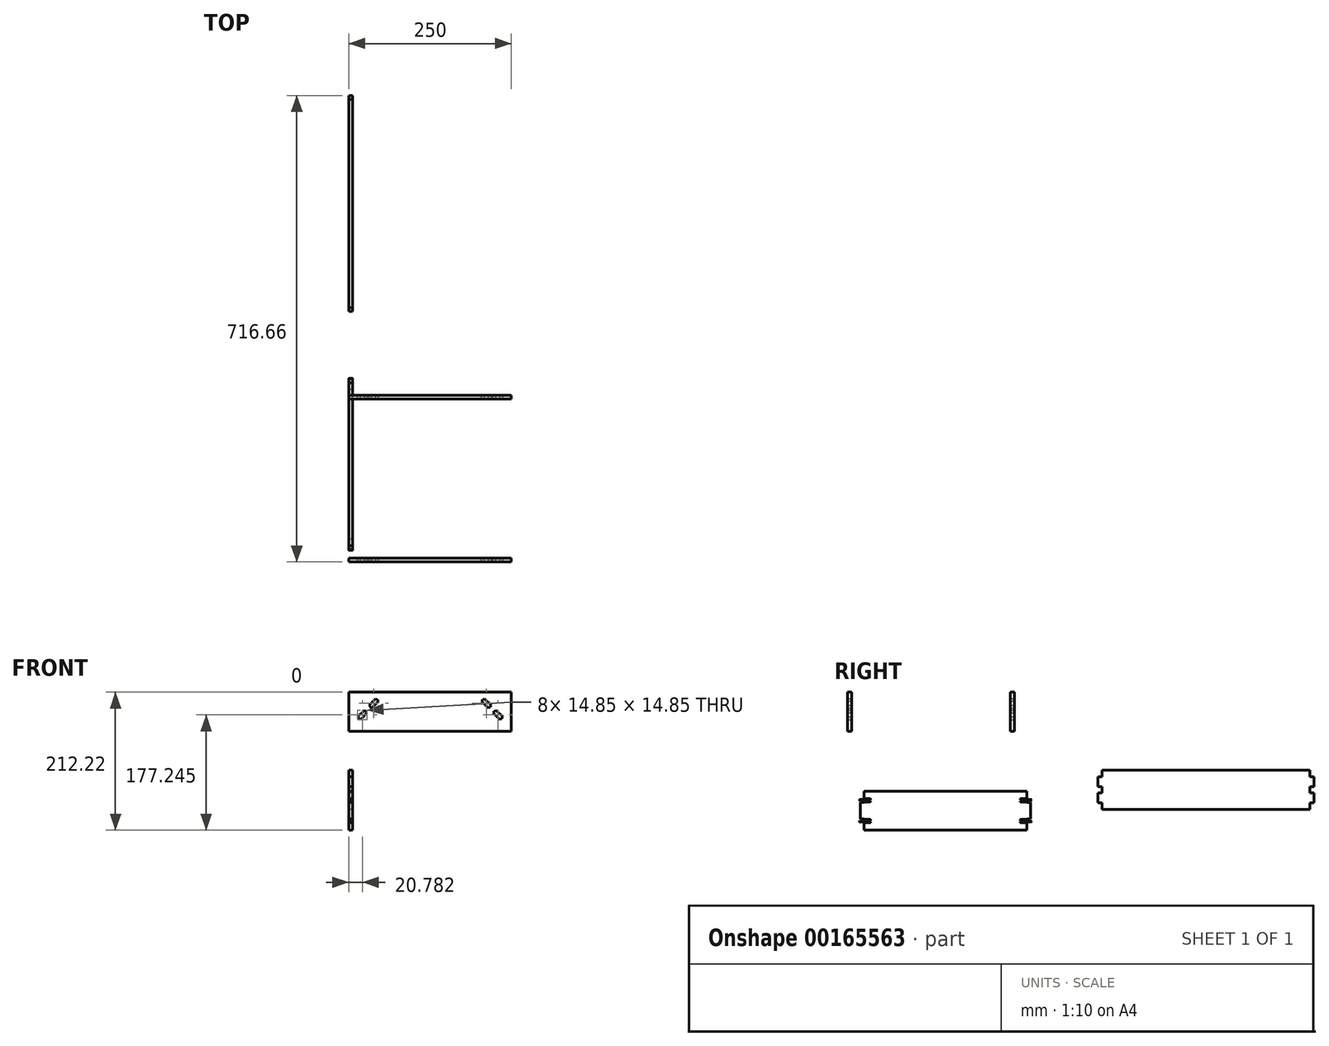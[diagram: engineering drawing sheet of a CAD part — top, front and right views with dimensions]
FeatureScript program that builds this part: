
annotation { "Feature Type Name" : "Feature", "Feature Type Description" : "" }
export const myFeature = defineFeature(function(context is Context, id is Id, definition is map)
    precondition{}
    {
        {
            assignVariable(context, id + "F0", {"name" : "t", "anyValue" : 6});
        }
        {
            assignVariable(context, id + "F1", {"name" : "w", "anyValue" : 250});
        }
        {
            var Q0;
            Q0=qCreatedBy(makeId("Front.planeOp"),FACE);
            var sketch = newSketch(context, id + "F2", { "sketchPlane" : qUnion([Q0])});
            skLineSegment(sketch, "E0.bottom", {"start": v(0, 0) * mm, "end": v(250, 0) * mm});
            skLineSegment(sketch, "E0.top", {"start": v(0, 60) * mm, "end": v(250, 60) * mm});
            skLineSegment(sketch, "E0.left", {"start": v(0, 0) * mm, "end": v(0, 60) * mm});
            skLineSegment(sketch, "E0.right", {"start": v(250, 0) * mm, "end": v(250, 60) * mm});
            skLineSegment(sketch, "E1.bottom", {"start": v(17.6, 17.6) * mm, "end": v(28.2, 28.2) * mm});
            skLineSegment(sketch, "E1.top", {"start": v(13.36, 21.84) * mm, "end": v(23.96, 32.45) * mm});
            skLineSegment(sketch, "E1.left", {"start": v(17.6, 17.6) * mm, "end": v(13.36, 21.84) * mm});
            skLineSegment(sketch, "E1.right", {"start": v(28.2, 28.2) * mm, "end": v(23.96, 32.45) * mm});
            skLineSegment(sketch, "E2.1.0.0", {"start": v(45.88, 45.88) * mm, "end": v(41.64, 50.13) * mm});
            skLineSegment(sketch, "E2.1.0.1", {"start": v(31.04, 39.52) * mm, "end": v(41.64, 50.13) * mm});
            skLineSegment(sketch, "E2.1.0.2", {"start": v(35.28, 35.28) * mm, "end": v(45.88, 45.88) * mm});
            skLineSegment(sketch, "E2.1.0.3", {"start": v(35.28, 35.28) * mm, "end": v(31.04, 39.52) * mm});
            skLineSegment(sketch, "E2.direction1", {"start": v(17.6, 17.6) * mm, "end": v(35.28, 35.28) * mm, "construction": true});
            skLineSegment(sketch, "E3", {"start": v(125, 48.06) * mm, "end": v(125, 16.76) * mm, "construction": true});
            skPoint(sketch, "E3.startSnap0", {"position": v(125, 60) * mm});
            skLineSegment(sketch, "E4.MirrorCS", {"start": v(221.8, 28.2) * mm, "end": v(226.04, 32.45) * mm});
            skLineSegment(sketch, "E5.MirrorCS", {"start": v(214.72, 35.28) * mm, "end": v(218.96, 39.52) * mm});
            skLineSegment(sketch, "E6.MirrorCS", {"start": v(232.4, 17.6) * mm, "end": v(221.8, 28.2) * mm});
            skLineSegment(sketch, "E7.MirrorCS", {"start": v(236.64, 21.84) * mm, "end": v(226.04, 32.45) * mm});
            skLineSegment(sketch, "E8.MirrorCS", {"start": v(232.4, 17.6) * mm, "end": v(236.64, 21.84) * mm});
            skLineSegment(sketch, "E9.MirrorCS", {"start": v(214.72, 35.28) * mm, "end": v(204.12, 45.88) * mm});
            skLineSegment(sketch, "E10.MirrorCS", {"start": v(204.12, 45.88) * mm, "end": v(208.36, 50.13) * mm});
            skLineSegment(sketch, "E11.MirrorCS", {"start": v(218.96, 39.52) * mm, "end": v(208.36, 50.13) * mm});
            skSolve(sketch);
        }
        {
            var Q0;
            Q0=makeQuery(id+"F2.imprint","IMPRINT",FACE,{"disambiguationData":[TD([[makeQuery(id+"F2.imprint","IMPRINT",EDGE,{"derivedFrom":sQuery(id+"F2.wireOp",EDGE,"E0.bottom")}),1.0]])]});
            extrude(context, id + "F3", {"entities" : qUnion([Q0]), "depth" : (getVariable(context, 't')) * mm});
        }
        {
            var Q0;
            Q0=makeQuery(id+"F3.opExtrude","SWEPT_BODY",BODY,{"disambiguationData":[OSD([sQuery(id+"F2.wireOp",EDGE,"E0.bottom"),sQuery(id+"F2.wireOp",EDGE,"E0.top"),sQuery(id+"F2.wireOp",EDGE,"E0.left"),sQuery(id+"F2.wireOp",EDGE,"E0.right")])]});
            transform(context, id + "F4", {"entities" : qUnion([Q0]), "transformType" : TransformType.TRANSLATION_3D, "dx" : 0 * mm, "dy" : (getVariable(context, 'w')) * mm, "dz" : 0 * mm, "makeCopy" : true});
        }
        {
            var Q0;
            Q0=qCreatedBy(makeId("Right.planeOp"),FACE);
            var sketch = newSketch(context, id + "F5", { "sketchPlane" : qUnion([Q0])});
            skLineSegment(sketch, "E12.bottom", {"start": v(19.14, -92.22) * mm, "end": v(269.14, -92.22) * mm});
            skLineSegment(sketch, "E12.top", {"start": v(19.14, -152.22) * mm, "end": v(269.14, -152.22) * mm});
            skLineSegment(sketch, "E12.left", {"start": v(19.14, -92.22) * mm, "end": v(19.14, -103.72) * mm});
            skLineSegment(sketch, "E13", {"start": v(19.14, -122.22) * mm, "end": v(269.14, -122.22) * mm, "construction": true});
            skLineSegment(sketch, "E14", {"start": v(144.14, -92.22) * mm, "end": v(144.14, -152.22) * mm, "construction": true});
            skLineSegment(sketch, "E15", {"start": v(13.14, -109.72) * mm, "end": v(19.14, -109.72) * mm});
            skLineSegment(sketch, "E16", {"start": v(19.14, -107.22) * mm, "end": v(13.14, -107.22) * mm});
            skLineSegment(sketch, "E17", {"start": v(13.14, -105.22) * mm, "end": v(19.14, -105.22) * mm});
            skLineSegment(sketch, "E18", {"start": v(12.05, -105.87) * mm, "end": v(13.14, -107.22) * mm});
            skLineSegment(sketch, "E19", {"start": v(19.14, -107.22) * mm, "end": v(28.38, -107.22) * mm});
            skLineSegment(sketch, "E20", {"start": v(28.38, -108.72) * mm, "end": v(19.14, -108.72) * mm});
            skLineSegment(sketch, "E21", {"start": v(19.14, -108.72) * mm, "end": v(19.14, -109.72) * mm});
            skLineSegment(sketch, "E22", {"start": v(19.14, -105.22) * mm, "end": v(28.38, -105.22) * mm});
            skArc(sketch, "E23", {"start": v(28.38, -105.22) * mm, "mid": v(29.13, -104.47) * mm, "end": v(28.38, -103.72) * mm});
            skArc(sketch, "E24", {"start": v(28.38, -108.72) * mm, "mid": v(29.13, -107.97) * mm, "end": v(28.38, -107.22) * mm});
            skPoint(sketch, "E25.visualSharp", {"position": v(12.44, -104.52) * mm});
            skPoint(sketch, "E26.visualSharp", {"position": v(11.9, -105.69) * mm});
            skLineSegment(sketch, "E27", {"start": v(13.14, -109.72) * mm, "end": v(13.14, -122.22) * mm});
            skLineSegment(sketch, "E28", {"start": v(13.14, -105.22) * mm, "end": v(12.66, -104.75) * mm});
            skLineSegment(sketch, "E29", {"start": v(12.02, -105.68) * mm, "end": v(12.33, -104.82) * mm});
            skArc(sketch, "E30.filletArc", {"start": v(12.66, -104.75) * mm, "mid": v(12.48, -104.7) * mm, "end": v(12.33, -104.82) * mm});
            skPoint(sketch, "E31.visualSharp", {"position": v(11.98, -105.78) * mm});
            skArc(sketch, "E31.filletArc", {"start": v(12.02, -105.68) * mm, "mid": v(12, -105.78) * mm, "end": v(12.05, -105.87) * mm});
            skLineSegment(sketch, "E32", {"start": v(13.14, -122.22) * mm, "end": v(13.14, -134.72) * mm});
            skLineSegment(sketch, "E33", {"start": v(13.14, -134.72) * mm, "end": v(19.14, -134.72) * mm});
            skPoint(sketch, "E34", {"position": v(19.14, -134.72) * mm});
            skLineSegment(sketch, "E35.trimOffspring", {"start": v(19.14, -134.72) * mm, "end": v(19.14, -134.72) * mm});
            skLineSegment(sketch, "E36", {"start": v(28.38, -103.72) * mm, "end": v(19.14, -103.72) * mm});
            skArc(sketch, "E37.MirrorCS", {"start": v(12.66, -139.69) * mm, "mid": v(12.48, -139.74) * mm, "end": v(12.33, -139.61) * mm});
            skLineSegment(sketch, "E38.MirrorCS", {"start": v(13.14, -139.2) * mm, "end": v(12.66, -139.69) * mm});
            skLineSegment(sketch, "E39.MirrorCS", {"start": v(12.02, -138.75) * mm, "end": v(12.33, -139.61) * mm});
            skArc(sketch, "E40.MirrorCS", {"start": v(12.02, -138.75) * mm, "mid": v(12, -138.65) * mm, "end": v(12.05, -138.56) * mm});
            skPoint(sketch, "E41.MirrorP", {"position": v(12.44, -139.9) * mm});
            skArc(sketch, "E42.MirrorCS", {"start": v(28.38, -135.7) * mm, "mid": v(29.13, -136.46) * mm, "end": v(28.38, -137.2) * mm});
            skLineSegment(sketch, "E43.MirrorCS", {"start": v(12.05, -138.56) * mm, "end": v(13.14, -137.2) * mm});
            skLineSegment(sketch, "E44.MirrorCS", {"start": v(19.14, -135.7) * mm, "end": v(19.14, -134.7) * mm});
            skArc(sketch, "E45.MirrorCS", {"start": v(28.38, -139.2) * mm, "mid": v(29.13, -139.96) * mm, "end": v(28.38, -140.7) * mm});
            skPoint(sketch, "E46.MirrorP", {"position": v(11.98, -138.65) * mm});
            skPoint(sketch, "E47.MirrorP", {"position": v(11.9, -138.74) * mm});
            skLineSegment(sketch, "E48.MirrorCS", {"start": v(19.14, -137.2) * mm, "end": v(13.14, -137.2) * mm});
            skLineSegment(sketch, "E49.MirrorCS", {"start": v(19.14, -137.2) * mm, "end": v(28.38, -137.2) * mm});
            skLineSegment(sketch, "E50.MirrorCS", {"start": v(28.38, -135.7) * mm, "end": v(19.14, -135.7) * mm});
            skLineSegment(sketch, "E51.MirrorCS", {"start": v(19.14, -139.2) * mm, "end": v(28.38, -139.2) * mm});
            skLineSegment(sketch, "E52.MirrorCS", {"start": v(19.14, -152.22) * mm, "end": v(19.14, -140.7) * mm});
            skLineSegment(sketch, "E53.MirrorCS", {"start": v(13.14, -139.2) * mm, "end": v(19.14, -139.2) * mm});
            skLineSegment(sketch, "E54.MirrorCS", {"start": v(28.38, -140.7) * mm, "end": v(19.14, -140.7) * mm});
            skLineSegment(sketch, "E55.trimOffspring", {"start": v(19.14, -140.7) * mm, "end": v(19.14, -152.22) * mm});
            skLineSegment(sketch, "E56.MirrorCS", {"start": v(275.14, -105.22) * mm, "end": v(275.62, -104.75) * mm});
            skArc(sketch, "E57.MirrorCS", {"start": v(276.26, -105.68) * mm, "mid": v(276.27, -105.78) * mm, "end": v(276.23, -105.87) * mm});
            skArc(sketch, "E58.MirrorCS", {"start": v(275.62, -139.69) * mm, "mid": v(275.8, -139.74) * mm, "end": v(275.95, -139.61) * mm});
            skLineSegment(sketch, "E59.MirrorCS", {"start": v(276.23, -105.87) * mm, "end": v(275.14, -107.22) * mm});
            skLineSegment(sketch, "E60.MirrorCS", {"start": v(276.26, -105.68) * mm, "end": v(275.95, -104.82) * mm});
            skArc(sketch, "E61.MirrorCS", {"start": v(275.62, -104.75) * mm, "mid": v(275.8, -104.7) * mm, "end": v(275.95, -104.82) * mm});
            skLineSegment(sketch, "E62.MirrorCS", {"start": v(276.23, -138.56) * mm, "end": v(275.14, -137.2) * mm});
            skLineSegment(sketch, "E63.MirrorCS", {"start": v(275.14, -139.2) * mm, "end": v(275.62, -139.69) * mm});
            skLineSegment(sketch, "E64.MirrorCS", {"start": v(276.26, -138.75) * mm, "end": v(275.95, -139.61) * mm});
            skArc(sketch, "E65.MirrorCS", {"start": v(276.26, -138.75) * mm, "mid": v(276.27, -138.65) * mm, "end": v(276.23, -138.56) * mm});
            skLineSegment(sketch, "E66.MirrorCS", {"start": v(269.14, -134.72) * mm, "end": v(269.14, -134.72) * mm});
            skLineSegment(sketch, "E67.MirrorCS", {"start": v(269.14, -135.7) * mm, "end": v(269.14, -134.7) * mm});
            skArc(sketch, "E68.MirrorCS", {"start": v(259.9, -108.72) * mm, "mid": v(259.15, -107.97) * mm, "end": v(259.9, -107.22) * mm});
            skLineSegment(sketch, "E69.MirrorCS", {"start": v(269.14, -107.22) * mm, "end": v(275.14, -107.22) * mm});
            skArc(sketch, "E70.MirrorCS", {"start": v(259.9, -135.7) * mm, "mid": v(259.15, -136.46) * mm, "end": v(259.9, -137.2) * mm});
            skLineSegment(sketch, "E71.MirrorCS", {"start": v(269.14, -108.72) * mm, "end": v(269.14, -109.72) * mm});
            skLineSegment(sketch, "E72.MirrorCS", {"start": v(275.14, -139.2) * mm, "end": v(269.14, -139.2) * mm});
            skLineSegment(sketch, "E73.MirrorCS", {"start": v(269.14, -152.22) * mm, "end": v(269.14, -140.7) * mm});
            skLineSegment(sketch, "E74.MirrorCS", {"start": v(269.14, -137.2) * mm, "end": v(275.14, -137.2) * mm});
            skArc(sketch, "E75.MirrorCS", {"start": v(259.9, -139.2) * mm, "mid": v(259.15, -139.96) * mm, "end": v(259.9, -140.7) * mm});
            skLineSegment(sketch, "E76.MirrorCS", {"start": v(269.14, -140.7) * mm, "end": v(269.14, -152.22) * mm});
            skArc(sketch, "E77.MirrorCS", {"start": v(259.9, -105.22) * mm, "mid": v(259.15, -104.47) * mm, "end": v(259.9, -103.72) * mm});
            skLineSegment(sketch, "E78.MirrorCS", {"start": v(269.14, -92.22) * mm, "end": v(269.14, -103.72) * mm});
            skLineSegment(sketch, "E79.MirrorCS", {"start": v(275.14, -105.22) * mm, "end": v(269.14, -105.22) * mm});
            skLineSegment(sketch, "E80.MirrorCS", {"start": v(275.14, -109.72) * mm, "end": v(269.14, -109.72) * mm});
            skPoint(sketch, "E81.MirrorP", {"position": v(275.84, -104.52) * mm});
            skLineSegment(sketch, "E82.MirrorCS", {"start": v(275.14, -134.72) * mm, "end": v(269.14, -134.72) * mm});
            skPoint(sketch, "E83.MirrorP", {"position": v(276.38, -105.69) * mm});
            skPoint(sketch, "E84.MirrorP", {"position": v(276.3, -105.78) * mm});
            skLineSegment(sketch, "E85.MirrorCS", {"start": v(259.9, -108.72) * mm, "end": v(269.14, -108.72) * mm});
            skPoint(sketch, "E86.MirrorP", {"position": v(275.84, -139.9) * mm});
            skPoint(sketch, "E87.MirrorP", {"position": v(276.3, -138.65) * mm});
            skLineSegment(sketch, "E88.MirrorCS", {"start": v(269.14, -107.22) * mm, "end": v(259.9, -107.22) * mm});
            skLineSegment(sketch, "E89.MirrorCS", {"start": v(269.14, -137.2) * mm, "end": v(259.9, -137.2) * mm});
            skPoint(sketch, "E90.MirrorP", {"position": v(276.38, -138.74) * mm});
            skLineSegment(sketch, "E91.MirrorCS", {"start": v(259.9, -140.7) * mm, "end": v(269.14, -140.7) * mm});
            skLineSegment(sketch, "E92.MirrorCS", {"start": v(275.14, -109.72) * mm, "end": v(275.14, -122.22) * mm});
            skLineSegment(sketch, "E93.MirrorCS", {"start": v(269.14, -139.2) * mm, "end": v(259.9, -139.2) * mm});
            skLineSegment(sketch, "E94.MirrorCS", {"start": v(259.9, -103.72) * mm, "end": v(269.14, -103.72) * mm});
            skPoint(sketch, "E95.MirrorP", {"position": v(269.14, -134.72) * mm});
            skLineSegment(sketch, "E96.MirrorCS", {"start": v(275.14, -122.22) * mm, "end": v(275.14, -134.72) * mm});
            skLineSegment(sketch, "E97.MirrorCS", {"start": v(269.14, -105.22) * mm, "end": v(259.9, -105.22) * mm});
            skLineSegment(sketch, "E98.MirrorCS", {"start": v(259.9, -135.7) * mm, "end": v(269.14, -135.7) * mm});
            skSolve(sketch);
        }
        {
            var Q0;
            Q0 = qSketchRegion(id + "F5", true);
            extrude(context, id + "F6", {"entities" : qUnion([Q0]), "depth" : 6 * mm});
        }
        {
            var Q0;
            Q0=qCreatedBy(makeId("Right.planeOp"),FACE);
            var sketch = newSketch(context, id + "F7", { "sketchPlane" : qUnion([Q0])});
            skLineSegment(sketch, "E99", {"start": v(378.66, -110.12) * mm, "end": v(378.66, -95.12) * mm});
            skLineSegment(sketch, "E100", {"start": v(378.66, -95.12) * mm, "end": v(384.66, -95.12) * mm});
            skLineSegment(sketch, "E101", {"start": v(384.66, -95.12) * mm, "end": v(384.66, -90.12) * mm});
            skLineSegment(sketch, "E102", {"start": v(384.66, -85.12) * mm, "end": v(378.66, -85.12) * mm});
            skLineSegment(sketch, "E103", {"start": v(378.66, -85.12) * mm, "end": v(378.66, -70.12) * mm});
            skLineSegment(sketch, "E104", {"start": v(378.66, -70.12) * mm, "end": v(384.66, -70.12) * mm});
            skLineSegment(sketch, "E105", {"start": v(384.66, -70.12) * mm, "end": v(384.66, -60.12) * mm});
            skLineSegment(sketch, "E106", {"start": v(378.66, -110.12) * mm, "end": v(384.66, -110.12) * mm});
            skLineSegment(sketch, "E107", {"start": v(384.66, -110.12) * mm, "end": v(384.66, -120.12) * mm});
            skLineSegment(sketch, "E108", {"start": v(384.66, -90.12) * mm, "end": v(389.84, -90.12) * mm, "construction": true});
            skPoint(sketch, "E108.endSnap0", {"position": v(384.66, -90.12) * mm});
            skLineSegment(sketch, "E109", {"start": v(384.66, -90.12) * mm, "end": v(384.66, -85.12) * mm});
            skLineSegment(sketch, "E110", {"start": v(384.66, -60.12) * mm, "end": v(544.66, -60.12) * mm});
            skLineSegment(sketch, "E111", {"start": v(384.66, -120.12) * mm, "end": v(544.66, -120.12) * mm});
            skLineSegment(sketch, "E112", {"start": v(544.66, -70) * mm, "end": v(544.66, -108.3) * mm, "construction": true});
            skLineSegment(sketch, "E113.MirrorCS", {"start": v(704.66, -90.12) * mm, "end": v(704.66, -85.12) * mm});
            skLineSegment(sketch, "E114.MirrorCS", {"start": v(704.66, -95.12) * mm, "end": v(704.66, -90.12) * mm});
            skLineSegment(sketch, "E115.MirrorCS", {"start": v(710.66, -70.12) * mm, "end": v(704.66, -70.12) * mm});
            skLineSegment(sketch, "E116.MirrorCS", {"start": v(710.66, -95.12) * mm, "end": v(704.66, -95.12) * mm});
            skLineSegment(sketch, "E117.MirrorCS", {"start": v(710.66, -110.12) * mm, "end": v(704.66, -110.12) * mm});
            skLineSegment(sketch, "E118.MirrorCS", {"start": v(704.66, -85.12) * mm, "end": v(710.66, -85.12) * mm});
            skLineSegment(sketch, "E119.MirrorCS", {"start": v(710.66, -85.12) * mm, "end": v(710.66, -70.12) * mm});
            skLineSegment(sketch, "E120.MirrorCS", {"start": v(704.66, -120.12) * mm, "end": v(544.66, -120.12) * mm});
            skLineSegment(sketch, "E121.MirrorCS", {"start": v(704.66, -110.12) * mm, "end": v(704.66, -120.12) * mm});
            skLineSegment(sketch, "E122.MirrorCS", {"start": v(704.66, -60.12) * mm, "end": v(544.66, -60.12) * mm});
            skLineSegment(sketch, "E123.MirrorCS", {"start": v(710.66, -110.12) * mm, "end": v(710.66, -95.12) * mm});
            skLineSegment(sketch, "E124.MirrorCS", {"start": v(704.66, -70.12) * mm, "end": v(704.66, -60.12) * mm});
            skSolve(sketch);
        }
        {
            var Q0;
            Q0=makeQuery(id+"F7.imprint","IMPRINT",FACE,{"disambiguationData":[TD([[makeQuery(id+"F7.imprint","IMPRINT",EDGE,{"derivedFrom":sQuery(id+"F7.wireOp",EDGE,"E99")}),-1.0]])]});
            extrude(context, id + "F8", {"entities" : qUnion([Q0]), "depth" : 6 * mm});
        }
    });
